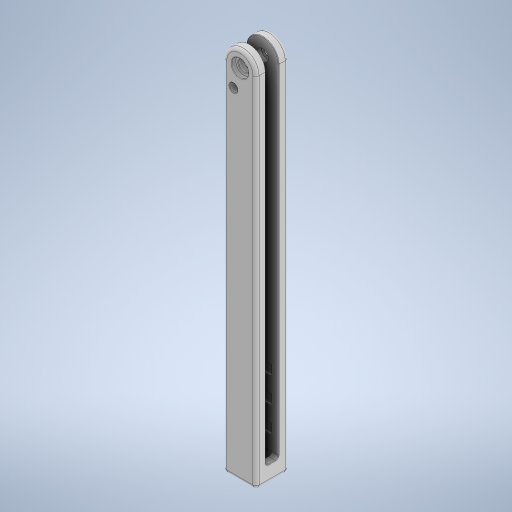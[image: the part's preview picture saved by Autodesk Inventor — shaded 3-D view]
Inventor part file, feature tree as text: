
AUTODESK INVENTOR PART (.ipt)
format: ipt  version: 2023.5 (Build 275446000, 446)  size: 393,216 bytes
history: native  units: mm
features: extrude x6, sketch x5, fillet x2, chamfer x2, plane x1, mirror x1, projected_geometry x1
ambient origin geometry x8: Origin, YZ Plane, XZ Plane, XY Plane, X Axis, Y Axis, Z Axis, Center Point
bodies: Solid1 (feature_tree)
feature tree (18):
  extrude  "Extrusion1"  Depth=12.7mm
  sketch  "Sketch2"  dims[d2=4.572mm d3=12.7mm d4=0.0mm]
  extrude  "Extrusion2"  Depth=12.7mm TaperAngle=0.0deg
  extrude  "Extrusion3"  Depth=5.08mm
  extrude  "Extrusion4"  Depth=120.048mm
  fillet  "Fillet1"  Radius=5.08mm
  extrude  "Extrusion6"  Depth=8.89mm TaperAngle=0.0deg
  plane  "Work Plane1"
  mirror  "Mirror1"
  extrude  "Extrusion7"  TaperAngle=0.0deg  [1 undecoded]
  chamfer  "Chamfer2"  Distance=3.175mm
  chamfer  "Chamfer3"  Distance=7.954mm
  fillet  "Fillet2"  Radius=2.54mm
  sketch  "Sketch1"  dims[d0=12.7mm d1=140.97mm]
  sketch  "Sketch3"  dims[d5=6.35mm d6=5.08mm]
  sketch  "Sketch5"  dims[d7=3.81mm d8=120.048mm d9=5.08mm]
  sketch  "Sketch6"  dims[d10=24.0mm d11=8.89mm d12=0.0mm d13=0.0mm d14=0.0mm d15=3.175mm d16=7.954mm d17=2.54mm d18=0.0mm d19=0.0mm d20=1.2mm d25=6.604mm d26=1.651mm d27=0.0mm d28=1.5mm d29=2.0mm d30=7.0mm d31=4.0mm d32=10.0mm d34=10.0mm d35=40.0mm d37=10.0mm d39=10.0mm d40=0.0mm d44=0.2mm d45=2.0mm d46=45.0deg d47=0.2mm d48=2.0mm d49=45.0deg d50=0.2mm]
  projected_geometry  "Projected Loop1"
note: 1 required parameter value undecoded (feature->parameter linkage not recoverable at this tier; creation-order binding heuristic only, values carry confidence <= 0.55)
